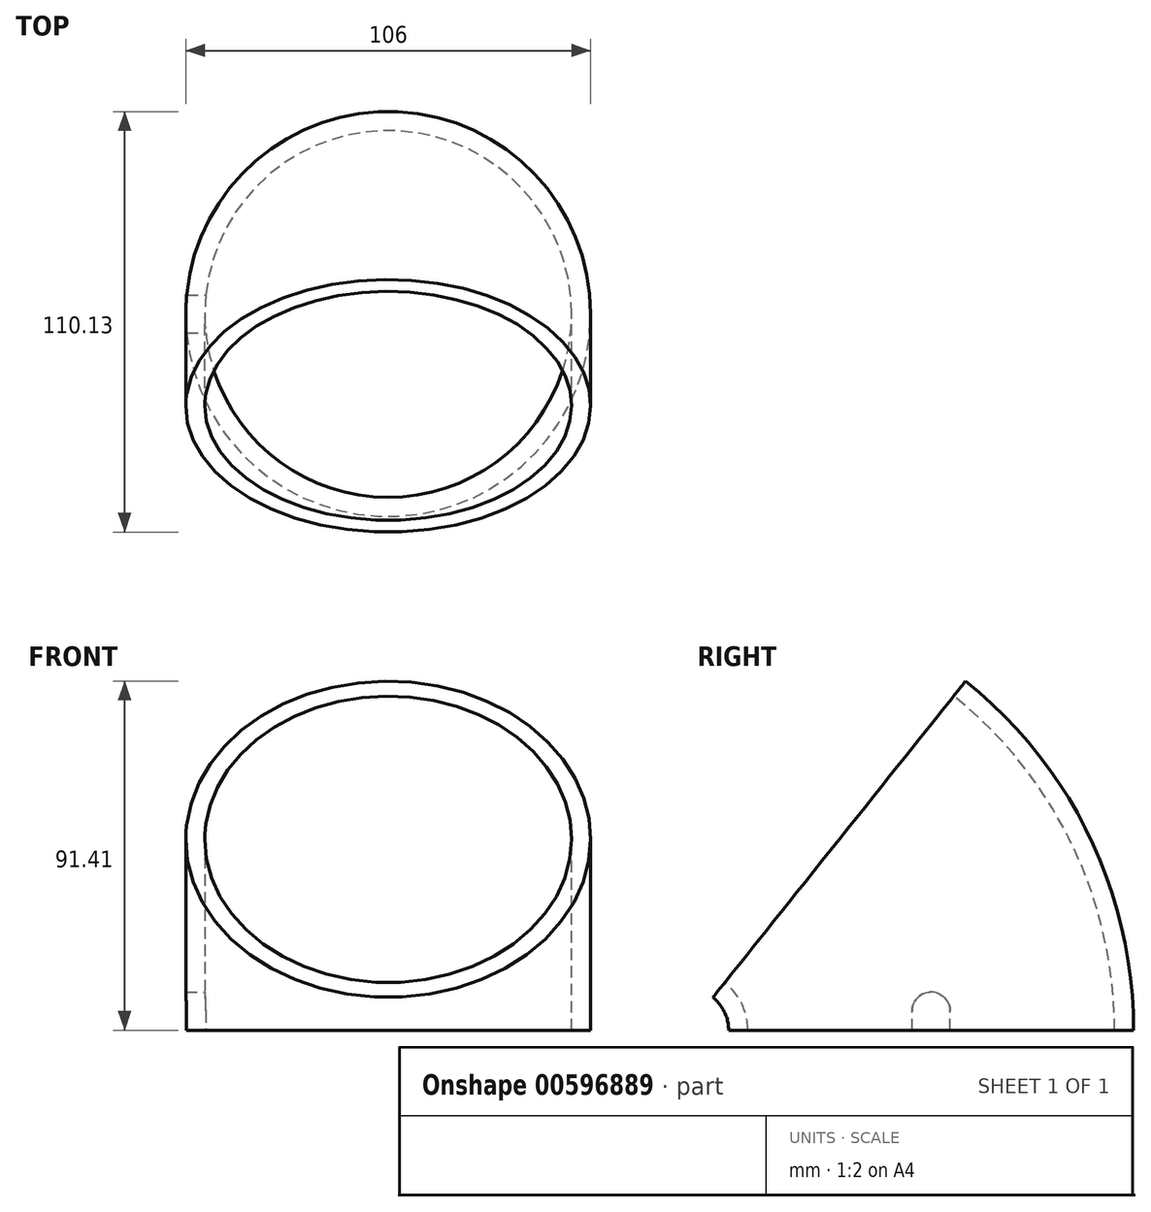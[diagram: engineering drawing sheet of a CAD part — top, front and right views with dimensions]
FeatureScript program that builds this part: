
annotation { "Feature Type Name" : "Feature", "Feature Type Description" : "" }
export const myFeature = defineFeature(function(context is Context, id is Id, definition is map)
    precondition{}
    {
        {
            var Q0;
            Q0=qCreatedBy(makeId("Top.planeOp"),FACE);
            var sketch = newSketch(context, id + "F0", { "sketchPlane" : qUnion([Q0])});
            skCircle(sketch, "E0", {"center": v(0, 0) * mm, "radius": 48 * mm});
            skCircle(sketch, "E1.0", {"center": v(0, 0) * mm, "radius": 53 * mm});
            skSolve(sketch);
        }
        {
            var Q0;
            Q0=qCreatedBy(makeId("Right.planeOp"),FACE);
            var sketch = newSketch(context, id + "F1", { "sketchPlane" : qUnion([Q0])});
            skPoint(sketch, "E2", {"position": v(-64, 0) * mm});
            skArc(sketch, "E3", {"start": v(0, 0) * mm, "mid": v(-6.33, 27.74) * mm, "end": v(-24.05, 50) * mm});
            skSolve(sketch);
        }
        {
            var Q0;
            Q0=makeQuery(id+"F0.imprint","IMPRINT",FACE,{"disambiguationData":[TD([[makeQuery(id+"F0.imprint","IMPRINT",EDGE,{"derivedFrom":sQuery(id+"F0.wireOp",EDGE,"E0")}),-1.0]])]});
            var Q1;
            Q1=sQuery(id+"F1.wireOp",EDGE,"E3");
            sweep(context, id + "F2", {"profiles" : qUnion([Q0]), "path" : qUnion([Q1])});
        }
        {
            var Q0;
            Q0=qCreatedBy(makeId("Right.planeOp"),FACE);
            var sketch = newSketch(context, id + "F3", { "sketchPlane" : qUnion([Q0])});
            skArc(sketch, "E4", {"start": v(-5, 0) * mm, "mid": v(0, -5) * mm, "end": v(5, 0) * mm});
            skLineSegment(sketch, "E5", {"start": v(0, 0) * mm, "end": v(0, 6.48) * mm, "construction": true});
            skArc(sketch, "E6", {"start": v(5, 5) * mm, "mid": v(0, 10) * mm, "end": v(-5, 5) * mm});
            skLineSegment(sketch, "E7", {"start": v(-5, 5) * mm, "end": v(-5, 0) * mm});
            skLineSegment(sketch, "E8", {"start": v(5, 5) * mm, "end": v(5, 0) * mm});
            skSolve(sketch);
        }
        {
            var Q0;
            Q0=makeQuery(id+"F3.imprint","IMPRINT",FACE,{"disambiguationData":[TD([[makeQuery(id+"F3.imprint","IMPRINT",EDGE,{"derivedFrom":sQuery(id+"F3.wireOp",EDGE,"E4")}),1.0]])]});
            extrude(context, id + "F4", {"entities" : qUnion([Q0]), "operationType" : NewBodyOperationType.REMOVE, "endBound" : BoundingType.THROUGH_ALL, "oppositeDirection" : true, "depth" : 25 * mm, "offsetDistance" : 25 * mm});
        }
    });
